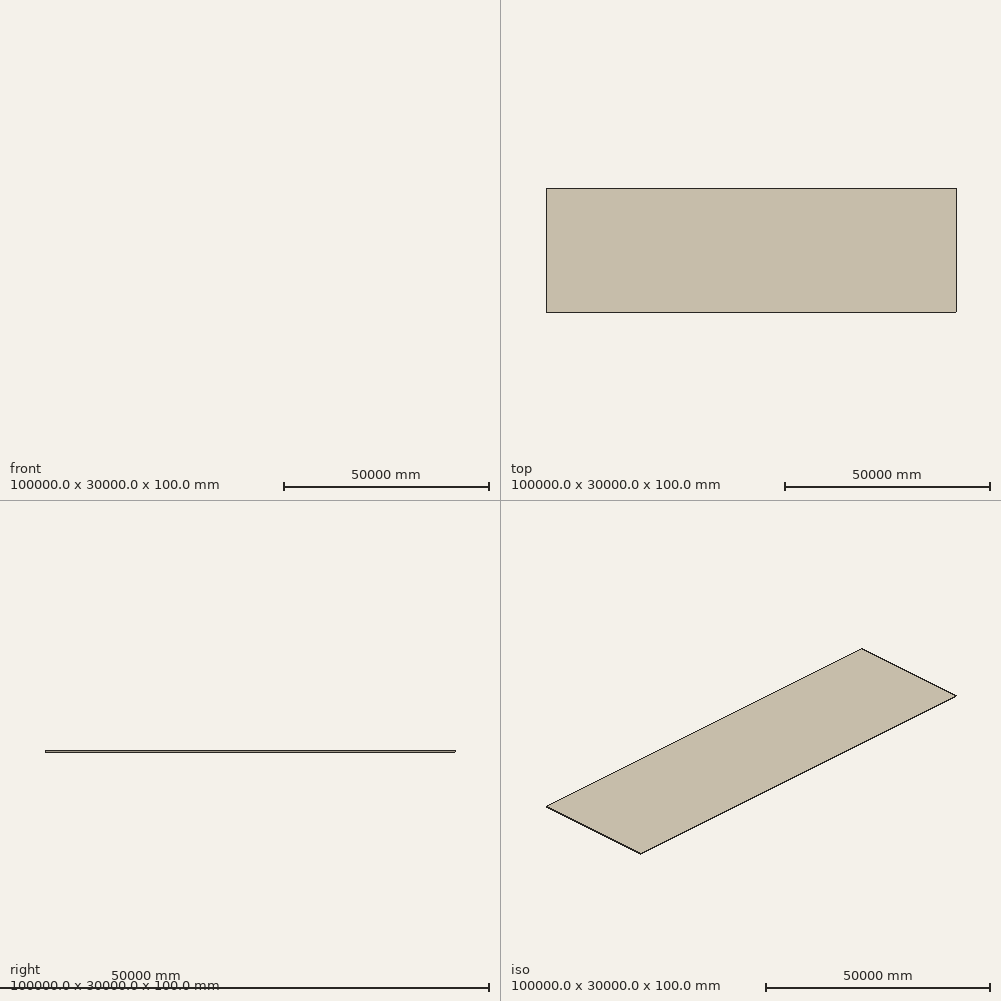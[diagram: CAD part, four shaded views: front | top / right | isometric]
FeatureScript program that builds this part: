
annotation { "Feature Type Name" : "Feature", "Feature Type Description" : "" }
export const myFeature = defineFeature(function(context is Context, id is Id, definition is map)
    precondition{}
    {
        {
            var Q0;
            Q0=qCreatedBy(makeId("Top.planeOp"),FACE);
            var sketch = newSketch(context, id + "F0", { "sketchPlane" : qUnion([Q0])});
            skLineSegment(sketch, "E0.bottom", {"start": v(-50000, 15000) * mm, "end": v(50000, 15000) * mm});
            skLineSegment(sketch, "E0.top", {"start": v(-50000, -15000) * mm, "end": v(50000, -15000) * mm});
            skLineSegment(sketch, "E0.left", {"start": v(-50000, 15000) * mm, "end": v(-50000, -15000) * mm});
            skLineSegment(sketch, "E0.right", {"start": v(50000, 15000) * mm, "end": v(50000, -15000) * mm});
            skPoint(sketch, "E0.middle", {"position": v(0, 0) * mm});
            skSolve(sketch);
        }
        {
            var Q0;
            Q0 = qSketchRegion(id + "F0", true);
            extrude(context, id + "F1", {"entities" : qUnion([Q0]), "depth" : 100 * mm, "offsetDistance" : 25 * mm});
        }
    });
